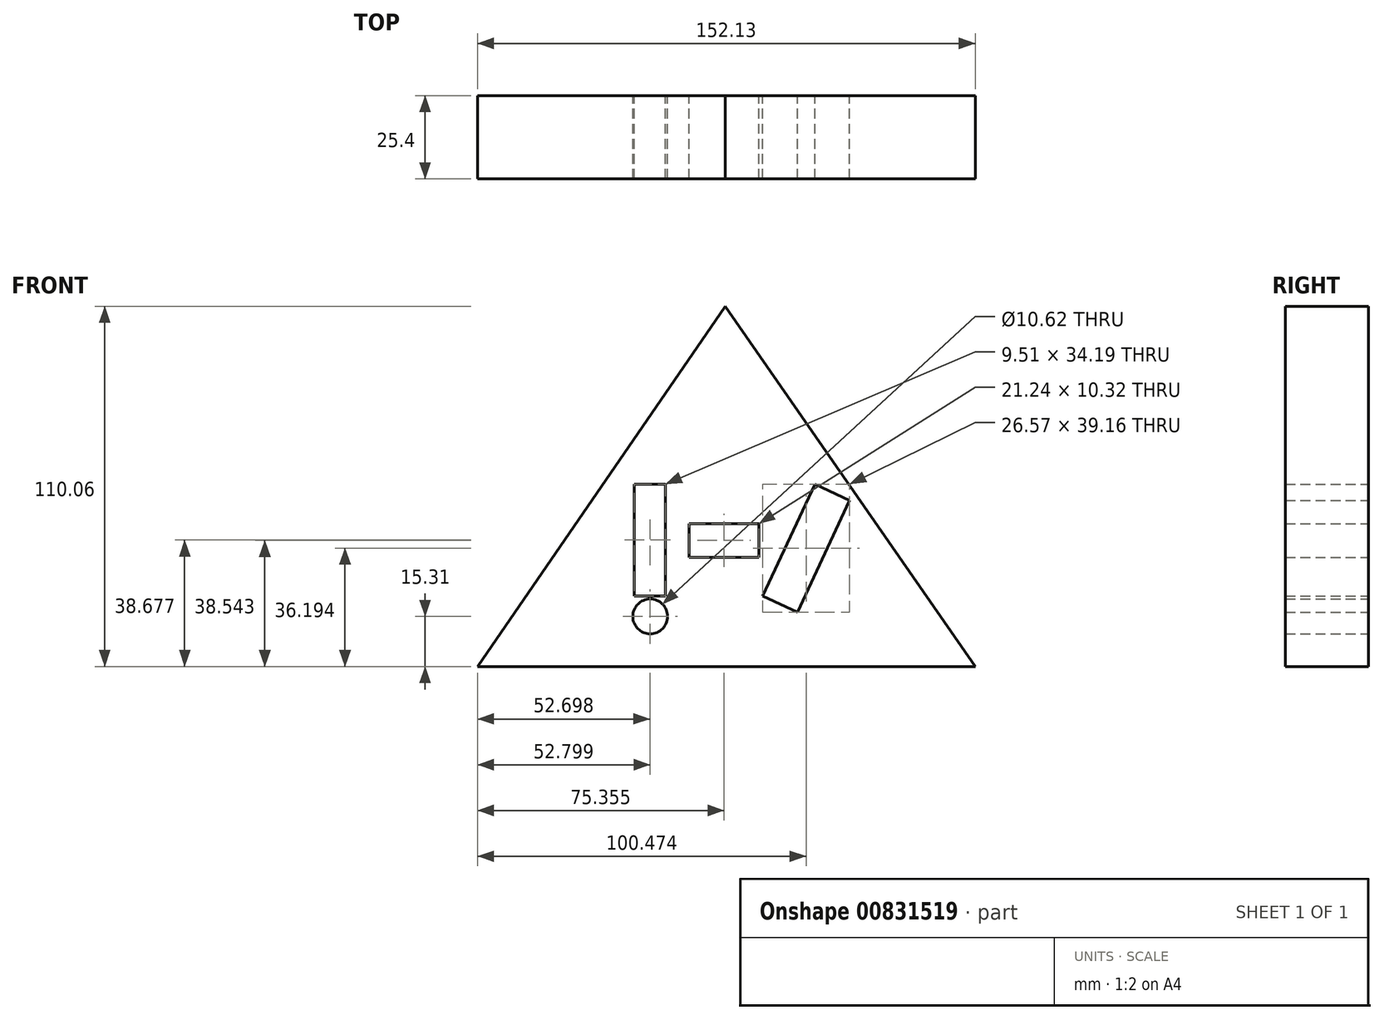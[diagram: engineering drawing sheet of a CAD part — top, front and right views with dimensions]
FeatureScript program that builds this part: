
annotation { "Feature Type Name" : "Feature", "Feature Type Description" : "" }
export const myFeature = defineFeature(function(context is Context, id is Id, definition is map)
    precondition{}
    {
        {
            var Q0;
            Q0=qCreatedBy(makeId("Front.planeOp"),FACE);
            var sketch = newSketch(context, id + "F0", { "sketchPlane" : qUnion([Q0])});
            skLineSegment(sketch, "E0.bottom", {"start": v(-27.82, 15.71) * mm, "end": v(-18.3, 15.71) * mm});
            skLineSegment(sketch, "E0.top", {"start": v(-27.82, -18.48) * mm, "end": v(-18.3, -18.48) * mm});
            skLineSegment(sketch, "E0.left", {"start": v(-27.82, 15.71) * mm, "end": v(-27.82, -18.48) * mm});
            skLineSegment(sketch, "E0.right", {"start": v(-18.3, 15.71) * mm, "end": v(-18.3, -18.48) * mm});
            skCircle(sketch, "E1", {"center": v(-22.96, -24.75) * mm, "radius": 5.31 * mm});
            skLineSegment(sketch, "E2.bottom", {"start": v(-11.03, 3.64) * mm, "end": v(10.22, 3.64) * mm});
            skLineSegment(sketch, "E2.top", {"start": v(-11.03, -6.68) * mm, "end": v(10.22, -6.68) * mm});
            skLineSegment(sketch, "E2.left", {"start": v(-11.03, 3.64) * mm, "end": v(-11.03, -6.68) * mm});
            skLineSegment(sketch, "E2.right", {"start": v(10.22, 3.64) * mm, "end": v(10.22, -6.68) * mm});
            skLineSegment(sketch, "E3", {"start": v(27.41, 15.71) * mm, "end": v(11.43, -18.48) * mm});
            skLineSegment(sketch, "E4", {"start": v(0, 70) * mm, "end": v(76.37, -40.06) * mm});
            skLineSegment(sketch, "E5", {"start": v(0, 70) * mm, "end": v(-75.76, -40.06) * mm});
            skLineSegment(sketch, "E6", {"start": v(-75.76, -40.06) * mm, "end": v(76.37, -40.06) * mm});
            skLineSegment(sketch, "E7", {"start": v(11.43, -18.48) * mm, "end": v(22.05, -23.44) * mm});
            skLineSegment(sketch, "E8", {"start": v(22.05, -23.44) * mm, "end": v(38, 10.66) * mm});
            skLineSegment(sketch, "E9", {"start": v(38, 10.66) * mm, "end": v(27.41, 15.71) * mm});
            skSolve(sketch);
        }
        {
            var Q0;
            Q0=makeQuery(id+"F0.imprint","IMPRINT",FACE,{"disambiguationData":[TD([[makeQuery(id+"F0.imprint","IMPRINT",EDGE,{"derivedFrom":sQuery(id+"F0.wireOp",EDGE,"E0.bottom")}),1.0]])]});
            extrude(context, id + "F1", {"entities" : qUnion([Q0]), "depth" : 25.4 * mm, "offsetDistance" : 25.4 * mm});
        }
    });
